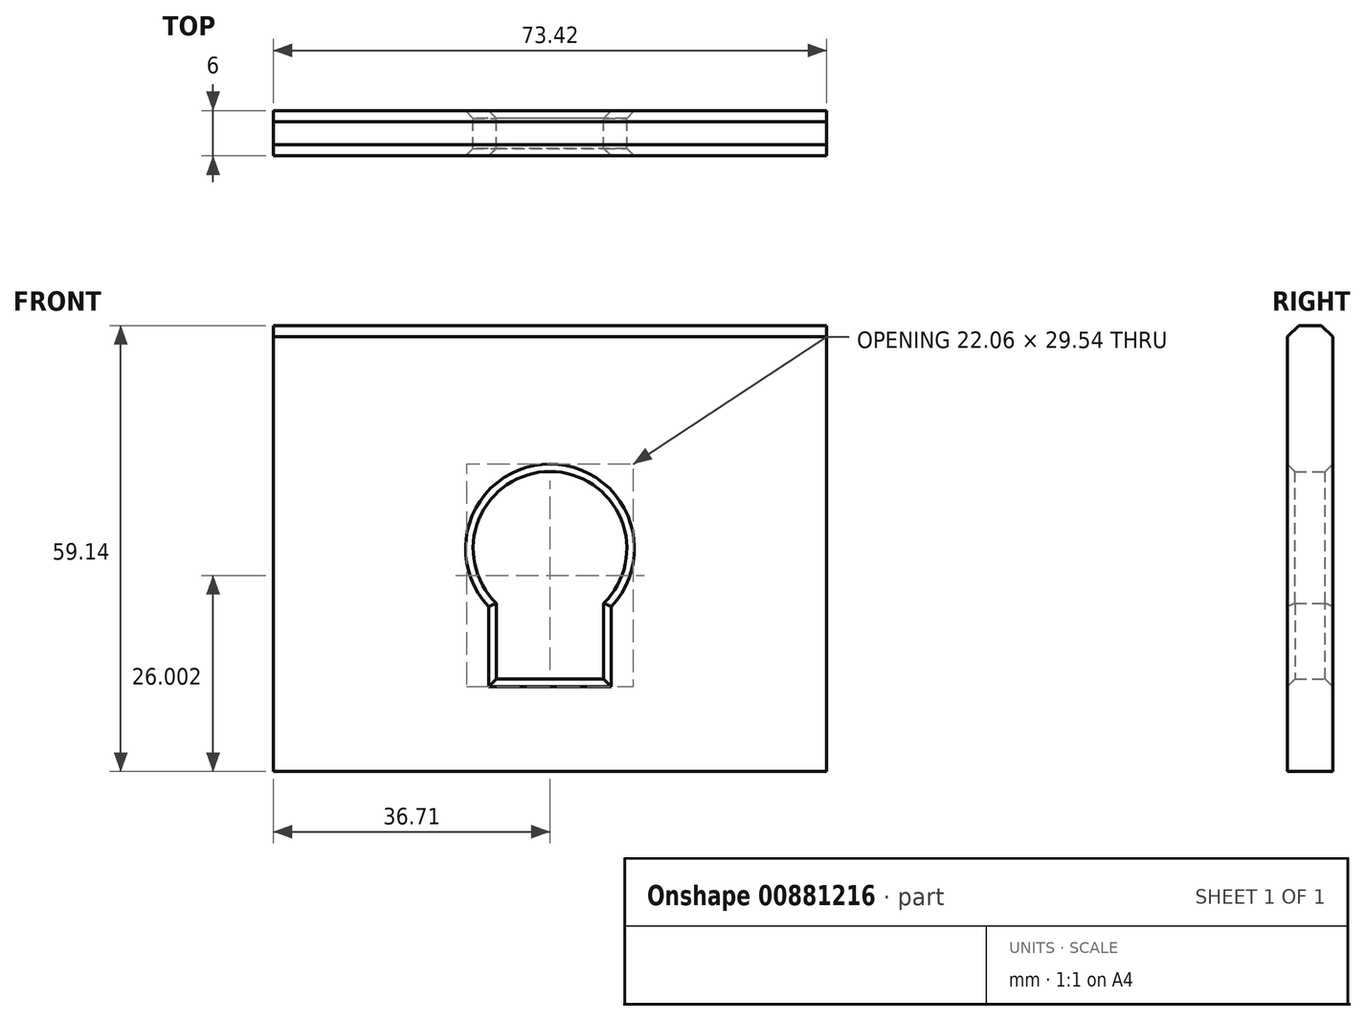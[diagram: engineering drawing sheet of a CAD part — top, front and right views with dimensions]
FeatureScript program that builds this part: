
annotation { "Feature Type Name" : "Feature", "Feature Type Description" : "" }
export const myFeature = defineFeature(function(context is Context, id is Id, definition is map)
    precondition{}
    {
        {
            var Q0;
            Q0=qCreatedBy(makeId("Front.planeOp"),FACE);
            var sketch = newSketch(context, id + "F0", { "sketchPlane" : qUnion([Q0])});
            skLineSegment(sketch, "E0", {"start": v(36.71, 29.57) * mm, "end": v(-36.71, 29.57) * mm});
            skLineSegment(sketch, "E1", {"start": v(-36.71, 29.57) * mm, "end": v(-36.71, -29.57) * mm});
            skLineSegment(sketch, "E2", {"start": v(36.71, -29.57) * mm, "end": v(-36.71, -29.57) * mm});
            skLineSegment(sketch, "E3", {"start": v(36.71, 29.57) * mm, "end": v(36.71, -29.57) * mm});
            skLineSegment(sketch, "E4", {"start": v(7.14, -17.34) * mm, "end": v(-7.14, -17.34) * mm});
            skArc(sketch, "E5", {"start": v(7.14, -7.29) * mm, "mid": v(0, 10.2) * mm, "end": v(-7.14, -7.29) * mm});
            skLineSegment(sketch, "E6", {"start": v(-7.14, -17.34) * mm, "end": v(-7.14, -7.29) * mm});
            skLineSegment(sketch, "E7", {"start": v(7.14, -17.34) * mm, "end": v(7.14, -7.29) * mm});
            skSolve(sketch);
        }
        {
            var Q0;
            Q0=makeQuery(id+"F0.imprint","IMPRINT",FACE,{"disambiguationData":[TD([[makeQuery(id+"F0.imprint","IMPRINT",EDGE,{"derivedFrom":sQuery(id+"F0.wireOp",EDGE,"E0")}),1.0]])]});
            extrude(context, id + "F1", {"entities" : qUnion([Q0]), "depth" : 6 * mm, "offsetDistance" : 25 * mm});
        }
        {
            var Q0;
            Q0=makeQuery(id+"F1.opExtrude","CAP_EDGE",EDGE,{"disambiguationData":[OSD([sQuery(id+"F0.wireOp",EDGE,"E5")])],"isStart":false});
            var Q1;
            Q1=makeQuery(id+"F1.opExtrude","CAP_EDGE",EDGE,{"disambiguationData":[OSD([sQuery(id+"F0.wireOp",EDGE,"E6")])],"isStart":false});
            var Q2;
            Q2=makeQuery(id+"F1.opExtrude","CAP_EDGE",EDGE,{"disambiguationData":[OSD([sQuery(id+"F0.wireOp",EDGE,"E4")])],"isStart":false});
            var Q3;
            Q3=makeQuery(id+"F1.opExtrude","CAP_EDGE",EDGE,{"disambiguationData":[OSD([sQuery(id+"F0.wireOp",EDGE,"E7")])],"isStart":false});
            var Q4;
            Q4=makeQuery(id+"F1.opExtrude","CAP_EDGE",EDGE,{"disambiguationData":[OSD([sQuery(id+"F0.wireOp",EDGE,"E4")])],"isStart":true});
            var Q5;
            Q5=makeQuery(id+"F1.opExtrude","CAP_EDGE",EDGE,{"disambiguationData":[OSD([sQuery(id+"F0.wireOp",EDGE,"E6")])],"isStart":true});
            var Q6;
            Q6=makeQuery(id+"F1.opExtrude","CAP_EDGE",EDGE,{"disambiguationData":[OSD([sQuery(id+"F0.wireOp",EDGE,"E5")])],"isStart":true});
            var Q7;
            Q7=makeQuery(id+"F1.opExtrude","CAP_EDGE",EDGE,{"disambiguationData":[OSD([sQuery(id+"F0.wireOp",EDGE,"E7")])],"isStart":true});
            chamfer(context, id + "F2", {"entities" : qUnion([Q0, Q1, Q2, Q3, Q4, Q5, Q6, Q7]), "width" : 1 * mm, "tangentPropagation" : true});
        }
        {
            var Q0;
            Q0=makeQuery(id+"F1.opExtrude","CAP_EDGE",EDGE,{"disambiguationData":[OSD([sQuery(id+"F0.wireOp",EDGE,"E0")])],"isStart":false});
            var Q1;
            Q1=makeQuery(id+"F1.opExtrude","CAP_EDGE",EDGE,{"disambiguationData":[OSD([sQuery(id+"F0.wireOp",EDGE,"E0")])],"isStart":true});
            chamfer(context, id + "F3", {"entities" : qUnion([Q0, Q1]), "width" : 1.5 * mm, "tangentPropagation" : true});
        }
    });
